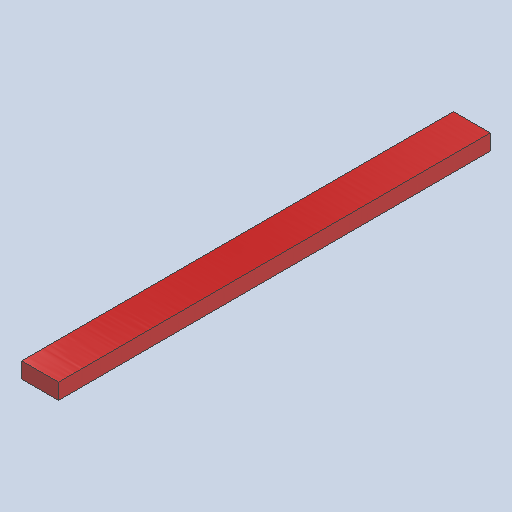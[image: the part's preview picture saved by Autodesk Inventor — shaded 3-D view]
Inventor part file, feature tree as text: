
AUTODESK INVENTOR PART (.ipt)
format: ipt  version: 2025.1 (Build 291241020, 241B)  size: 250,368 bytes
history: native  units: in
note: dims shown in document units (in); Inventor stores cm internally (conversion verified against a paired STEP export)
features: other x3, plane x1, extrude x1, sketch x1
ambient origin geometry x8: Origin, YZ Plane, XZ Plane, XY Plane, X Axis, Y Axis, Z Axis, Center Point
bodies: Solid1 (feature_tree)
feature tree (6):
  plane  "Work Plane1"
  extrude  "Extrusion1"  Depth=3.5in
  sketch  "Sketch1"  dims[d0=1.5in d1=3.5in d2=41.0in d3=0.0in]
  other  "Finish1"
  other  "Assembly2"
  other  "8'x2x4:1"
